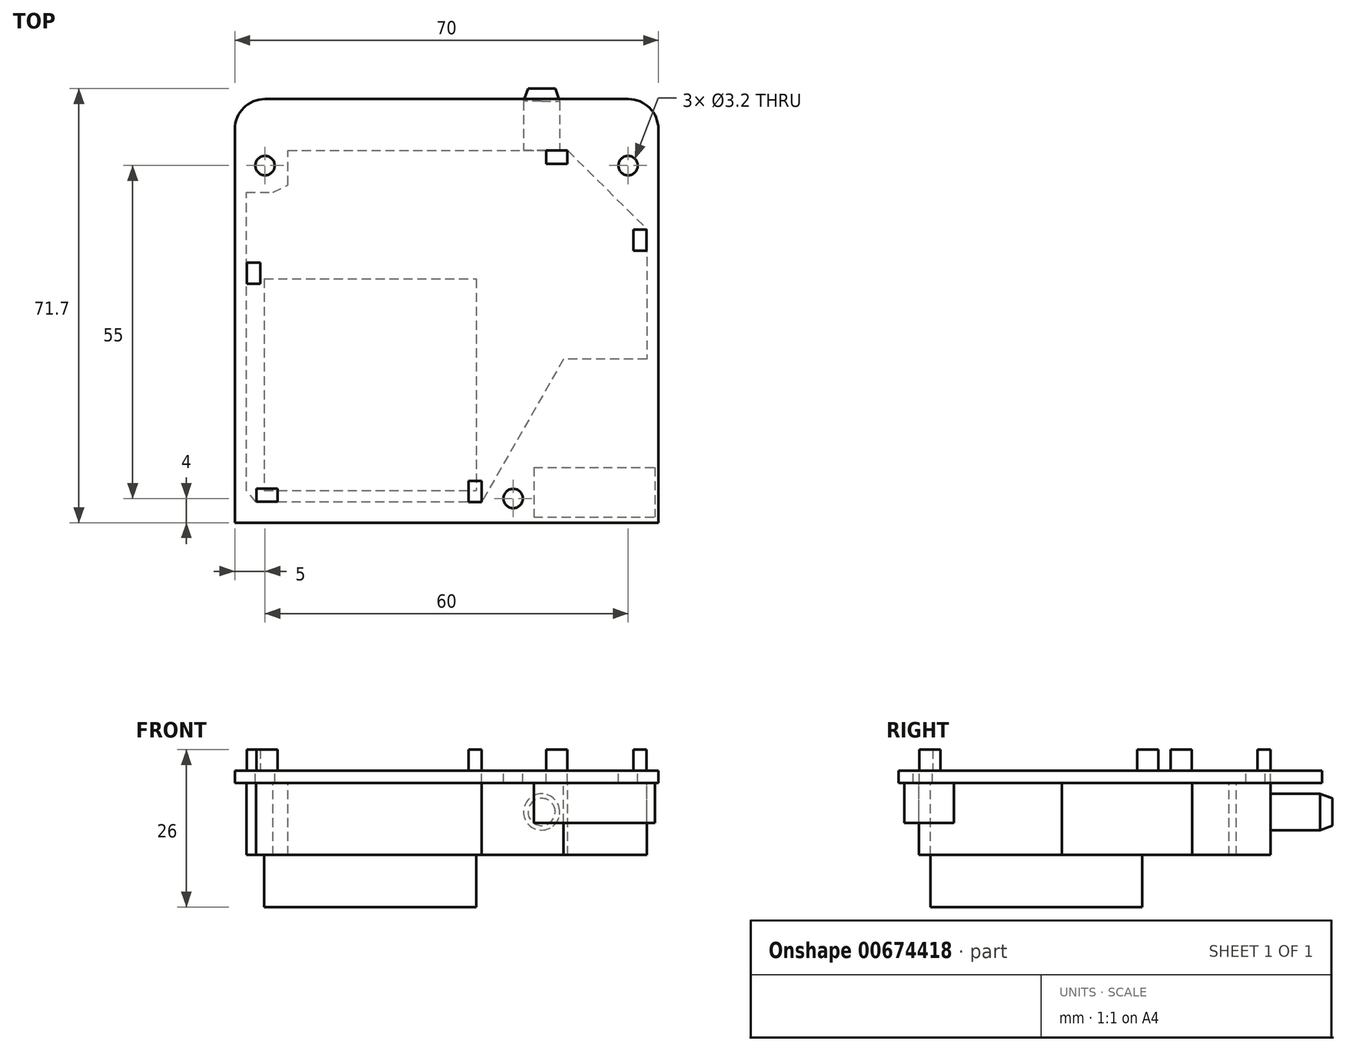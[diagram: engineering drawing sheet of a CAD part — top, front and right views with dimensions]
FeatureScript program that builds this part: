
annotation { "Feature Type Name" : "Feature", "Feature Type Description" : "" }
export const myFeature = defineFeature(function(context is Context, id is Id, definition is map)
    precondition{}
    {
        {
            var Q0;
            Q0=qCreatedBy(makeId("Top.planeOp"),FACE);
            var sketch = newSketch(context, id + "F0", { "sketchPlane" : qUnion([Q0])});
            skLineSegment(sketch, "E0.bottom", {"start": v(30, 35) * mm, "end": v(-30, 35) * mm});
            skLineSegment(sketch, "E0.top", {"start": v(35, -35) * mm, "end": v(-35, -35) * mm});
            skLineSegment(sketch, "E0.left", {"start": v(35, 30) * mm, "end": v(35, -35) * mm});
            skLineSegment(sketch, "E0.right", {"start": v(-35, 30) * mm, "end": v(-35, -35) * mm});
            skPoint(sketch, "E0.middle", {"position": v(0, 0) * mm});
            skCircle(sketch, "E1", {"center": v(-30, 24) * mm, "radius": 1.6 * mm});
            skCircle(sketch, "E2", {"center": v(30, 24) * mm, "radius": 1.6 * mm});
            skCircle(sketch, "E3", {"center": v(11, -31) * mm, "radius": 1.6 * mm});
            skLineSegment(sketch, "E4", {"start": v(-35, 24) * mm, "end": v(35, 24) * mm, "construction": true});
            skLineSegment(sketch, "E5", {"start": v(-26.2, 26.5) * mm, "end": v(20, 26.5) * mm});
            skLineSegment(sketch, "E6", {"start": v(20, 26.5) * mm, "end": v(33.1, 13.5) * mm});
            skLineSegment(sketch, "E7", {"start": v(33.1, 13.5) * mm, "end": v(33.1, -8) * mm});
            skLineSegment(sketch, "E8", {"start": v(33.1, -8) * mm, "end": v(19.3, -8) * mm});
            skLineSegment(sketch, "E9", {"start": v(19.3, -8) * mm, "end": v(5.8, -31.6) * mm});
            skLineSegment(sketch, "E10", {"start": v(5.8, -31.6) * mm, "end": v(-31.5, -31.6) * mm});
            skLineSegment(sketch, "E11", {"start": v(-31.5, -31.6) * mm, "end": v(-33.1, -29.7) * mm});
            skLineSegment(sketch, "E12", {"start": v(-33.1, -29.7) * mm, "end": v(-33.1, 19.6) * mm});
            skLineSegment(sketch, "E13", {"start": v(-33.1, 19.6) * mm, "end": v(-28.7, 19.6) * mm});
            skLineSegment(sketch, "E14", {"start": v(-28.7, 19.6) * mm, "end": v(-26.2, 20.8) * mm});
            skLineSegment(sketch, "E15", {"start": v(-26.2, 20.8) * mm, "end": v(-26.2, 26.5) * mm});
            skCircle(sketch, "E16", {"center": v(4.2, 30.7) * mm, "radius": 1.75 * mm, "construction": true});
            skCircle(sketch, "E17", {"center": v(30, 24) * mm, "radius": 2.85 * mm, "construction": true});
            skCircle(sketch, "E18", {"center": v(-30, 24) * mm, "radius": 2.85 * mm, "construction": true});
            skCircle(sketch, "E19", {"center": v(11, -31) * mm, "radius": 2.85 * mm, "construction": true});
            skCircle(sketch, "E20", {"center": v(4.2, 30.7) * mm, "radius": 3.5 * mm, "construction": true});
            skLineSegment(sketch, "E21.bottom", {"start": v(14.4, -25.85) * mm, "end": v(34.4, -25.85) * mm});
            skLineSegment(sketch, "E21.top", {"start": v(14.4, -34.05) * mm, "end": v(34.4, -34.05) * mm});
            skLineSegment(sketch, "E21.left", {"start": v(14.4, -25.85) * mm, "end": v(14.4, -34.05) * mm});
            skLineSegment(sketch, "E21.right", {"start": v(34.4, -25.85) * mm, "end": v(34.4, -34.05) * mm});
            skCircle(sketch, "E22", {"center": v(16.78, -27.49) * mm, "radius": 0.5 * mm, "construction": true});
            skCircle(sketch, "E23.1.0.0", {"center": v(19.32, -27.49) * mm, "radius": 0.5 * mm, "construction": true});
            skCircle(sketch, "E23.2.0.0", {"center": v(21.86, -27.49) * mm, "radius": 0.5 * mm, "construction": true});
            skCircle(sketch, "E24.0.3.0", {"center": v(24.4, -27.49) * mm, "radius": 0.5 * mm, "construction": true});
            skCircle(sketch, "E24.0.4.0", {"center": v(26.94, -27.49) * mm, "radius": 0.5 * mm, "construction": true});
            skCircle(sketch, "E24.0.5.0", {"center": v(29.48, -27.49) * mm, "radius": 0.5 * mm, "construction": true});
            skCircle(sketch, "E24.0.6.0", {"center": v(32.02, -27.49) * mm, "radius": 0.5 * mm, "construction": true});
            skPoint(sketch, "E25.visualSharp", {"position": v(-35, 35) * mm});
            skArc(sketch, "E25.filletArc", {"start": v(-30, 35) * mm, "mid": v(-33.54, 33.54) * mm, "end": v(-35, 30) * mm});
            skPoint(sketch, "E26.visualSharp", {"position": v(35, 35) * mm});
            skArc(sketch, "E26.filletArc", {"start": v(35, 30) * mm, "mid": v(33.54, 33.54) * mm, "end": v(30, 35) * mm});
            skLineSegment(sketch, "E27.bottom", {"start": v(-30.13, 5.28) * mm, "end": v(4.87, 5.28) * mm});
            skLineSegment(sketch, "E27.top", {"start": v(-30.13, -29.72) * mm, "end": v(4.87, -29.72) * mm});
            skLineSegment(sketch, "E27.left", {"start": v(-30.13, 5.28) * mm, "end": v(-30.13, -29.72) * mm});
            skLineSegment(sketch, "E27.right", {"start": v(4.87, 5.28) * mm, "end": v(4.87, -29.72) * mm});
            skLineSegment(sketch, "E28.bottom", {"start": v(33.05, 9.95) * mm, "end": v(30.85, 9.95) * mm});
            skLineSegment(sketch, "E28.top", {"start": v(33.05, 13.45) * mm, "end": v(30.85, 13.45) * mm});
            skLineSegment(sketch, "E28.left", {"start": v(33.05, 9.95) * mm, "end": v(33.05, 13.45) * mm});
            skLineSegment(sketch, "E28.right", {"start": v(30.85, 9.95) * mm, "end": v(30.85, 13.45) * mm});
            skPoint(sketch, "E28.middle", {"position": v(31.95, 11.7) * mm});
            skLineSegment(sketch, "E29.bottom", {"start": v(19.93, 24.3) * mm, "end": v(16.43, 24.3) * mm});
            skLineSegment(sketch, "E29.top", {"start": v(19.93, 26.5) * mm, "end": v(16.43, 26.5) * mm});
            skLineSegment(sketch, "E29.left", {"start": v(19.93, 24.3) * mm, "end": v(19.93, 26.5) * mm});
            skLineSegment(sketch, "E29.right", {"start": v(16.43, 24.3) * mm, "end": v(16.43, 26.5) * mm});
            skPoint(sketch, "E29.middle", {"position": v(18.18, 25.4) * mm});
            skLineSegment(sketch, "E30.bottom", {"start": v(-27.93, -31.55) * mm, "end": v(-31.43, -31.55) * mm});
            skLineSegment(sketch, "E30.top", {"start": v(-27.93, -29.35) * mm, "end": v(-31.43, -29.35) * mm});
            skLineSegment(sketch, "E30.left", {"start": v(-27.93, -31.55) * mm, "end": v(-27.93, -29.35) * mm});
            skLineSegment(sketch, "E30.right", {"start": v(-31.43, -31.55) * mm, "end": v(-31.43, -29.35) * mm});
            skPoint(sketch, "E30.middle", {"position": v(-29.68, -30.45) * mm});
            skLineSegment(sketch, "E31.bottom", {"start": v(-30.8, 4.45) * mm, "end": v(-33, 4.45) * mm});
            skLineSegment(sketch, "E31.top", {"start": v(-30.8, 7.95) * mm, "end": v(-33, 7.95) * mm});
            skLineSegment(sketch, "E31.left", {"start": v(-30.8, 4.45) * mm, "end": v(-30.8, 7.95) * mm});
            skLineSegment(sketch, "E31.right", {"start": v(-33, 4.45) * mm, "end": v(-33, 7.95) * mm});
            skPoint(sketch, "E31.middle", {"position": v(-31.9, 6.2) * mm});
            skLineSegment(sketch, "E32.bottom", {"start": v(5.8, -31.6) * mm, "end": v(3.6, -31.6) * mm});
            skLineSegment(sketch, "E32.top", {"start": v(5.8, -28.1) * mm, "end": v(3.6, -28.1) * mm});
            skLineSegment(sketch, "E32.left", {"start": v(5.8, -31.6) * mm, "end": v(5.8, -28.1) * mm});
            skLineSegment(sketch, "E32.right", {"start": v(3.6, -31.6) * mm, "end": v(3.6, -28.1) * mm});
            skPoint(sketch, "E32.middle", {"position": v(4.7, -29.84) * mm});
            skSolve(sketch);
        }
        {
            var Q0;
            Q0=makeQuery(id+"F0.imprint","IMPRINT",FACE,{"disambiguationData":[TD([[makeQuery(id+"F0.imprint","IMPRINT",EDGE,{"derivedFrom":sQuery(id+"F0.wireOp",EDGE,"E0.bottom")}),1.0]])]});
            var Q1;
            Q1=makeQuery(id+"F0.imprint","IMPRINT",FACE,{"disambiguationData":[TD([[makeQuery(id+"F0.imprint","IMPRINT",EDGE,{"derivedFrom":sQuery(id+"F0.wireOp",EDGE,"E5")}),-1.0]])]});
            var Q2;
            Q2=makeQuery(id+"F0.imprint","IMPRINT",FACE,{"disambiguationData":[TD([[makeQuery(id+"F0.imprint","IMPRINT",EDGE,{"derivedFrom":sQuery(id+"F0.wireOp",EDGE,"E27.bottom")}),-1.0]])]});
            var Q3;
            Q3=makeQuery(id+"F0.imprint","IMPRINT",FACE,{"disambiguationData":[TD([[makeQuery(id+"F0.imprint","IMPRINT",EDGE,{"derivedFrom":sQuery(id+"F0.wireOp",EDGE,"E21.bottom")}),-1.0]])]});
            var Q4;
            Q4=makeQuery(id+"F0.imprint","IMPRINT",FACE,{"disambiguationData":[TD([[makeQuery(id+"F0.imprint","IMPRINT",EDGE,{"derivedFrom":sQuery(id+"F0.wireOp",EDGE,"E28.bottom")}),-1.0]])]});
            var Q5;
            {var subQ5=sQuery(id+"F0.wireOp",EDGE,"E29.bottom");Q5=makeQuery(id+"F0.imprint","IMPRINT",FACE,{"disambiguationData":[TD([[makeQuery(id+"F0.imprint","IMPRINT",EDGE,{"derivedFrom":subQ5}),-1.0]])]});}
            var Q6;
            {var subQ3=sQuery(id+"F0.wireOp",EDGE,"E9");var subQ11=sQuery(id+"F0.wireOp",EDGE,"E32.left");var subQ12=makeQuery(id+"F0.imprint","INTERSECT",VERTEX,{"derivedFrom":[subQ3,subQ11]});Q6=makeQuery(id+"F0.imprint","IMPRINT",FACE,{"disambiguationData":[TD([[makeQuery(id+"F0.imprint","IMPRINT",EDGE,{"disambiguationData":[TD([[subQ12,-1.0]])],"derivedFrom":subQ3}),-1.0]])]});}
            var Q7;
            {var subQ0=sQuery(id+"F0.wireOp",EDGE,"E30.bottom");Q7=makeQuery(id+"F0.imprint","IMPRINT",FACE,{"disambiguationData":[TD([[makeQuery(id+"F0.imprint","IMPRINT",EDGE,{"derivedFrom":subQ0}),-1.0]])]});}
            var Q8;
            Q8=makeQuery(id+"F0.imprint","IMPRINT",FACE,{"disambiguationData":[TD([[makeQuery(id+"F0.imprint","IMPRINT",EDGE,{"derivedFrom":sQuery(id+"F0.wireOp",EDGE,"E31.bottom")}),-1.0]])]});
            extrude(context, id + "F1", {"entities" : qUnion([Q0, Q1, Q2, Q3, Q4, Q5, Q6, Q7, Q8]), "oppositeDirection" : true, "depth" : 2 * mm, "offsetDistance" : 25 * mm});
        }
        {
            var Q0;
            Q0=makeQuery(id+"F0.imprint","IMPRINT",FACE,{"disambiguationData":[TD([[makeQuery(id+"F0.imprint","IMPRINT",EDGE,{"derivedFrom":sQuery(id+"F0.wireOp",EDGE,"E5")}),-1.0]])]});
            var Q1;
            Q1=makeQuery(id+"F0.imprint","IMPRINT",FACE,{"disambiguationData":[TD([[makeQuery(id+"F0.imprint","IMPRINT",EDGE,{"derivedFrom":sQuery(id+"F0.wireOp",EDGE,"E27.bottom")}),-1.0]])]});
            var Q2;
            {var subQ3=sQuery(id+"F0.wireOp",EDGE,"E9");var subQ11=sQuery(id+"F0.wireOp",EDGE,"E32.left");var subQ12=makeQuery(id+"F0.imprint","INTERSECT",VERTEX,{"derivedFrom":[subQ3,subQ11]});Q2=makeQuery(id+"F0.imprint","IMPRINT",FACE,{"disambiguationData":[TD([[makeQuery(id+"F0.imprint","IMPRINT",EDGE,{"disambiguationData":[TD([[subQ12,-1.0]])],"derivedFrom":subQ3}),-1.0]])]});}
            var Q3;
            Q3=makeQuery(id+"F0.imprint","IMPRINT",FACE,{"disambiguationData":[TD([[makeQuery(id+"F0.imprint","IMPRINT",EDGE,{"derivedFrom":sQuery(id+"F0.wireOp",EDGE,"E31.bottom")}),-1.0]])]});
            var Q4;
            {var subQ5=sQuery(id+"F0.wireOp",EDGE,"E29.bottom");Q4=makeQuery(id+"F0.imprint","IMPRINT",FACE,{"disambiguationData":[TD([[makeQuery(id+"F0.imprint","IMPRINT",EDGE,{"derivedFrom":subQ5}),-1.0]])]});}
            var Q5;
            Q5=makeQuery(id+"F0.imprint","IMPRINT",FACE,{"disambiguationData":[TD([[makeQuery(id+"F0.imprint","IMPRINT",EDGE,{"derivedFrom":sQuery(id+"F0.wireOp",EDGE,"E28.bottom")}),-1.0]])]});
            var Q6;
            {var subQ0=sQuery(id+"F0.wireOp",EDGE,"E27.right");var subQ1=sQuery(id+"F0.wireOp",EDGE,"E27.top");var subQ2=makeQuery(id+"F0.imprint","INTERSECT",VERTEX,{"derivedFrom":[subQ1,subQ0]});Q6=makeQuery(id+"F0.imprint","IMPRINT",FACE,{"disambiguationData":[TD([[makeQuery(id+"F0.imprint","IMPRINT",EDGE,{"disambiguationData":[TD([[subQ2,1.0]])],"derivedFrom":subQ1}),1.0]])]});}
            var Q7;
            {var subQ0=sQuery(id+"F0.wireOp",EDGE,"E30.bottom");Q7=makeQuery(id+"F0.imprint","IMPRINT",FACE,{"disambiguationData":[TD([[makeQuery(id+"F0.imprint","IMPRINT",EDGE,{"derivedFrom":subQ0}),-1.0]])]});}
            var Q8;
            {var subQ0=sQuery(id+"F0.wireOp",EDGE,"E27.left");var subQ1=sQuery(id+"F0.wireOp",EDGE,"E27.top");var subQ2=makeQuery(id+"F0.imprint","INTERSECT",VERTEX,{"derivedFrom":[subQ1,subQ0]});Q8=makeQuery(id+"F0.imprint","IMPRINT",FACE,{"disambiguationData":[TD([[makeQuery(id+"F0.imprint","IMPRINT",EDGE,{"disambiguationData":[TD([[subQ2,-1.0]])],"derivedFrom":subQ1}),1.0]])]});}
            extrude(context, id + "F2", {"entities" : qUnion([Q0, Q1, Q2, Q3, Q4, Q5, Q6, Q7, Q8]), "operationType" : NewBodyOperationType.ADD, "oppositeDirection" : true, "depth" : 13.9 * mm, "offsetDistance" : 25 * mm});
        }
        {
            var Q0;
            Q0=makeQuery(id+"F0.imprint","IMPRINT",FACE,{"disambiguationData":[TD([[makeQuery(id+"F0.imprint","IMPRINT",EDGE,{"derivedFrom":sQuery(id+"F0.wireOp",EDGE,"E21.bottom")}),-1.0]])]});
            extrude(context, id + "F3", {"entities" : qUnion([Q0]), "operationType" : NewBodyOperationType.ADD, "oppositeDirection" : true, "depth" : 8.6 * mm, "offsetDistance" : 25 * mm});
        }
        {
            var Q0;
            Q0=makeQuery(id+"F0.imprint","IMPRINT",FACE,{"disambiguationData":[TD([[makeQuery(id+"F0.imprint","IMPRINT",EDGE,{"derivedFrom":sQuery(id+"F0.wireOp",EDGE,"E27.bottom")}),-1.0]])]});
            var Q1;
            {var subQ0=sQuery(id+"F0.wireOp",EDGE,"E27.right");var subQ1=sQuery(id+"F0.wireOp",EDGE,"E27.top");var subQ2=makeQuery(id+"F0.imprint","INTERSECT",VERTEX,{"derivedFrom":[subQ1,subQ0]});Q1=makeQuery(id+"F0.imprint","IMPRINT",FACE,{"disambiguationData":[TD([[makeQuery(id+"F0.imprint","IMPRINT",EDGE,{"disambiguationData":[TD([[subQ2,1.0]])],"derivedFrom":subQ1}),1.0]])]});}
            var Q2;
            {var subQ0=sQuery(id+"F0.wireOp",EDGE,"E27.left");var subQ1=sQuery(id+"F0.wireOp",EDGE,"E27.top");var subQ2=makeQuery(id+"F0.imprint","INTERSECT",VERTEX,{"derivedFrom":[subQ1,subQ0]});Q2=makeQuery(id+"F0.imprint","IMPRINT",FACE,{"disambiguationData":[TD([[makeQuery(id+"F0.imprint","IMPRINT",EDGE,{"disambiguationData":[TD([[subQ2,-1.0]])],"derivedFrom":subQ1}),1.0]])]});}
            extrude(context, id + "F4", {"entities" : qUnion([Q0, Q1, Q2]), "operationType" : NewBodyOperationType.ADD, "oppositeDirection" : true, "depth" : 22.5 * mm, "offsetDistance" : 25 * mm});
        }
        {
            var Q0;
            Q0=makeQuery(id+"F2.opExtrude","SWEPT_FACE",FACE,{"disambiguationData":[OSD([sQuery(id+"F0.wireOp",EDGE,"E5")])]});
            var sketch = newSketch(context, id + "F5", { "sketchPlane" : qUnion([Q0])});
            skCircle(sketch, "E33", {"center": v(-15.7, -6.8) * mm, "radius": 3 * mm});
            skSolve(sketch);
        }
        {
            var Q0;
            Q0=makeQuery(id+"F5.imprint","IMPRINT",FACE,{"disambiguationData":[TD([[makeQuery(id+"F5.imprint","IMPRINT",EDGE,{"derivedFrom":sQuery(id+"F5.wireOp",EDGE,"E33")}),1.0]])]});
            extrude(context, id + "F6", {"entities" : qUnion([Q0]), "operationType" : NewBodyOperationType.ADD, "depth" : 10.2 * mm, "offsetDistance" : 25 * mm});
        }
        {
            var Q0;
            Q0=makeQuery(id+"F6.opExtrude","CAP_EDGE",EDGE,{"disambiguationData":[OSD([sQuery(id+"F5.wireOp",EDGE,"E33")])],"isStart":false});
            chamfer(context, id + "F7", {"entities" : qUnion([Q0]), "chamferType" : ChamferType.OFFSET_ANGLE, "width" : 0.75 * mm, "oppositeDirection" : false, "angle" : 70 * degree, "tangentPropagation" : true});
        }
        {
            var Q0;
            {var subQ0=sQuery(id+"F0.wireOp",EDGE,"E30.bottom");Q0=makeQuery(id+"F0.imprint","IMPRINT",FACE,{"disambiguationData":[TD([[makeQuery(id+"F0.imprint","IMPRINT",EDGE,{"derivedFrom":subQ0}),-1.0]])]});}
            var Q1;
            {var subQ3=sQuery(id+"F0.wireOp",EDGE,"E9");var subQ11=sQuery(id+"F0.wireOp",EDGE,"E32.left");var subQ12=makeQuery(id+"F0.imprint","INTERSECT",VERTEX,{"derivedFrom":[subQ3,subQ11]});Q1=makeQuery(id+"F0.imprint","IMPRINT",FACE,{"disambiguationData":[TD([[makeQuery(id+"F0.imprint","IMPRINT",EDGE,{"disambiguationData":[TD([[subQ12,-1.0]])],"derivedFrom":subQ3}),-1.0]])]});}
            var Q2;
            {var subQ0=sQuery(id+"F0.wireOp",EDGE,"E27.right");var subQ1=sQuery(id+"F0.wireOp",EDGE,"E27.top");var subQ2=makeQuery(id+"F0.imprint","INTERSECT",VERTEX,{"derivedFrom":[subQ1,subQ0]});Q2=makeQuery(id+"F0.imprint","IMPRINT",FACE,{"disambiguationData":[TD([[makeQuery(id+"F0.imprint","IMPRINT",EDGE,{"disambiguationData":[TD([[subQ2,1.0]])],"derivedFrom":subQ1}),1.0]])]});}
            var Q3;
            {var subQ0=sQuery(id+"F0.wireOp",EDGE,"E27.left");var subQ1=sQuery(id+"F0.wireOp",EDGE,"E27.top");var subQ2=makeQuery(id+"F0.imprint","INTERSECT",VERTEX,{"derivedFrom":[subQ1,subQ0]});Q3=makeQuery(id+"F0.imprint","IMPRINT",FACE,{"disambiguationData":[TD([[makeQuery(id+"F0.imprint","IMPRINT",EDGE,{"disambiguationData":[TD([[subQ2,-1.0]])],"derivedFrom":subQ1}),1.0]])]});}
            var Q4;
            Q4=makeQuery(id+"F0.imprint","IMPRINT",FACE,{"disambiguationData":[TD([[makeQuery(id+"F0.imprint","IMPRINT",EDGE,{"derivedFrom":sQuery(id+"F0.wireOp",EDGE,"E31.bottom")}),-1.0]])]});
            var Q5;
            {var subQ5=sQuery(id+"F0.wireOp",EDGE,"E29.bottom");Q5=makeQuery(id+"F0.imprint","IMPRINT",FACE,{"disambiguationData":[TD([[makeQuery(id+"F0.imprint","IMPRINT",EDGE,{"derivedFrom":subQ5}),-1.0]])]});}
            var Q6;
            Q6=makeQuery(id+"F0.imprint","IMPRINT",FACE,{"disambiguationData":[TD([[makeQuery(id+"F0.imprint","IMPRINT",EDGE,{"derivedFrom":sQuery(id+"F0.wireOp",EDGE,"E28.bottom")}),-1.0]])]});
            extrude(context, id + "F8", {"entities" : qUnion([Q0, Q1, Q2, Q3, Q4, Q5, Q6]), "operationType" : NewBodyOperationType.ADD, "depth" : 3.5 * mm, "offsetDistance" : 25 * mm});
        }
    });
